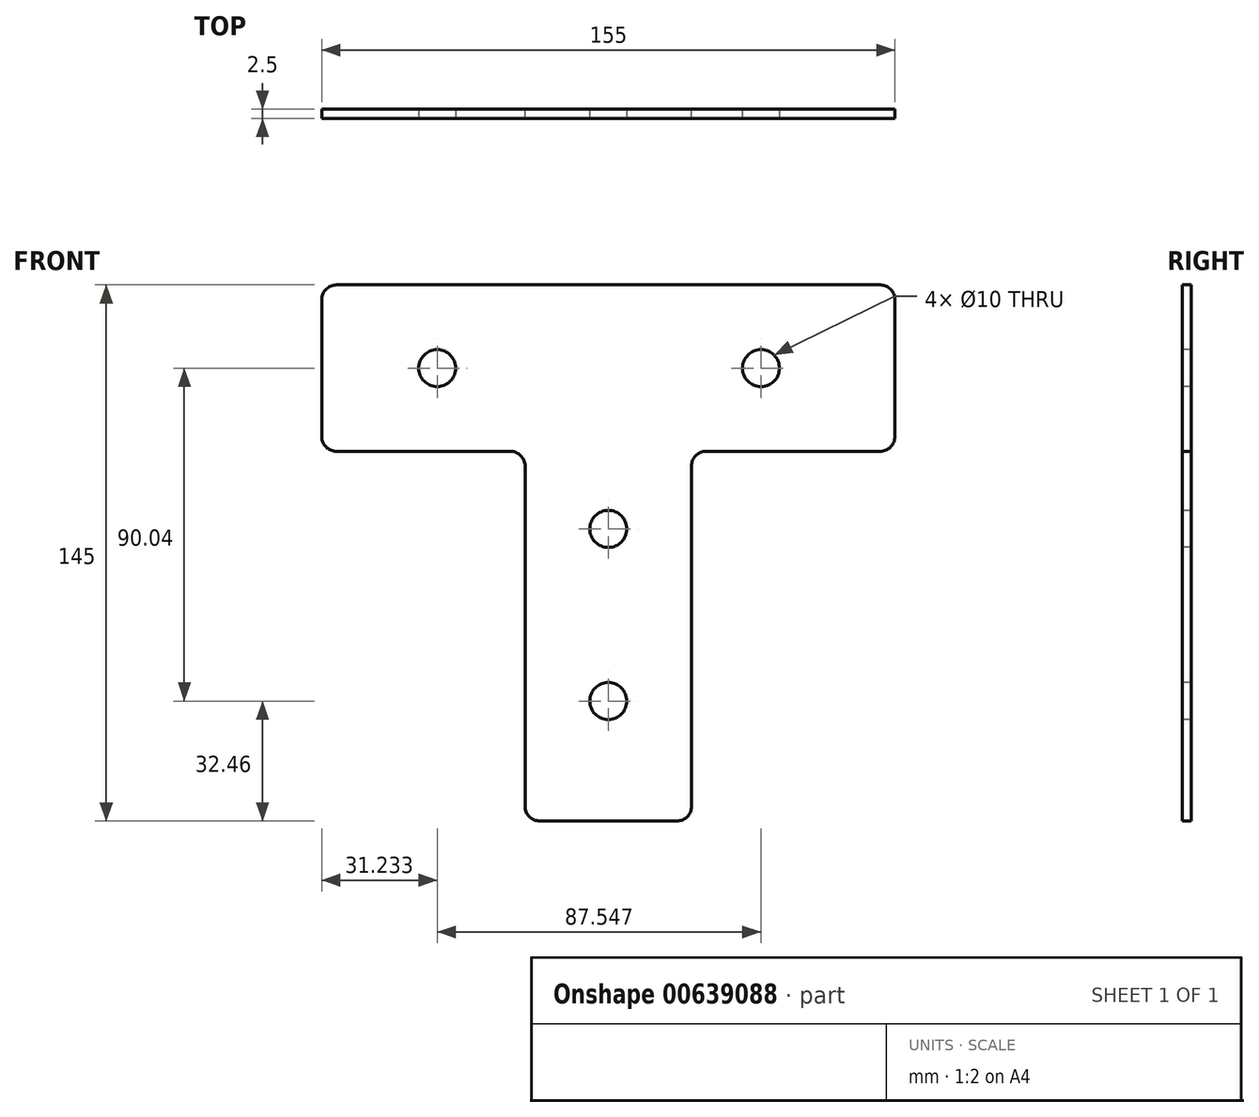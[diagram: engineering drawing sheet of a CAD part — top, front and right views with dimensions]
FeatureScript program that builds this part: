
annotation { "Feature Type Name" : "Feature", "Feature Type Description" : "" }
export const myFeature = defineFeature(function(context is Context, id is Id, definition is map)
    precondition{}
    {
        {
            var Q0;
            Q0=qCreatedBy(makeId("Front.planeOp"),FACE);
            var sketch = newSketch(context, id + "F0", { "sketchPlane" : qUnion([Q0])});
            skLineSegment(sketch, "E0.bottom", {"start": v(73.5, 22.5) * mm, "end": v(-73.5, 22.5) * mm});
            skLineSegment(sketch, "E0.top", {"start": v(77.5, -22.5) * mm, "end": v(22.5, -22.5) * mm});
            skLineSegment(sketch, "E0.left", {"start": v(77.5, 18.5) * mm, "end": v(77.5, -18.5) * mm});
            skLineSegment(sketch, "E0.right", {"start": v(-77.5, 18.5) * mm, "end": v(-77.5, -18.5) * mm});
            skPoint(sketch, "E0.middle", {"position": v(0, 0) * mm});
            skLineSegment(sketch, "E1", {"start": v(73.5, -22.5) * mm, "end": v(26.5, -22.5) * mm});
            skLineSegment(sketch, "E2", {"start": v(22.5, -26.5) * mm, "end": v(22.5, -118.5) * mm});
            skLineSegment(sketch, "E3", {"start": v(18.5, -122.5) * mm, "end": v(-18.5, -122.5) * mm});
            skLineSegment(sketch, "E4", {"start": v(-22.5, -118.5) * mm, "end": v(-22.5, -26.5) * mm});
            skLineSegment(sketch, "E5", {"start": v(-22.5, -22.5) * mm, "end": v(-77.5, -22.5) * mm});
            skLineSegment(sketch, "E6.trimOffspring", {"start": v(-26.5, -22.5) * mm, "end": v(-73.5, -22.5) * mm});
            skPoint(sketch, "E7.visualSharp", {"position": v(-77.5, 22.5) * mm});
            skArc(sketch, "E7.filletArc", {"start": v(-73.5, 22.5) * mm, "mid": v(-76.33, 21.33) * mm, "end": v(-77.5, 18.5) * mm});
            skPoint(sketch, "E8.visualSharp", {"position": v(-77.5, -22.5) * mm});
            skArc(sketch, "E8.filletArc", {"start": v(-77.5, -18.5) * mm, "mid": v(-76.33, -21.33) * mm, "end": v(-73.5, -22.5) * mm});
            skPoint(sketch, "E9.visualSharp", {"position": v(77.5, 22.5) * mm});
            skArc(sketch, "E9.filletArc", {"start": v(77.5, 18.5) * mm, "mid": v(76.33, 21.33) * mm, "end": v(73.5, 22.5) * mm});
            skPoint(sketch, "E10.visualSharp", {"position": v(77.5, -22.5) * mm});
            skArc(sketch, "E10.filletArc", {"start": v(73.5, -22.5) * mm, "mid": v(76.33, -21.33) * mm, "end": v(77.5, -18.5) * mm});
            skPoint(sketch, "E11.visualSharp", {"position": v(22.5, -22.5) * mm});
            skArc(sketch, "E11.filletArc", {"start": v(26.5, -22.5) * mm, "mid": v(23.67, -23.67) * mm, "end": v(22.5, -26.5) * mm});
            skPoint(sketch, "E12.visualSharp", {"position": v(22.5, -122.5) * mm});
            skArc(sketch, "E12.filletArc", {"start": v(18.5, -122.5) * mm, "mid": v(21.33, -121.33) * mm, "end": v(22.5, -118.5) * mm});
            skPoint(sketch, "E13.visualSharp", {"position": v(-22.5, -122.5) * mm});
            skArc(sketch, "E13.filletArc", {"start": v(-22.5, -118.5) * mm, "mid": v(-21.33, -121.33) * mm, "end": v(-18.5, -122.5) * mm});
            skPoint(sketch, "E14.visualSharp", {"position": v(-22.5, -22.5) * mm});
            skArc(sketch, "E14.filletArc", {"start": v(-22.5, -26.5) * mm, "mid": v(-23.67, -23.67) * mm, "end": v(-26.5, -22.5) * mm});
            skSolve(sketch);
        }
        {
            var Q0;
            Q0 = qSketchRegion(id + "F0", true);
            extrude(context, id + "F1", {"entities" : qUnion([Q0]), "depth" : 2.5 * mm, "offsetDistance" : 25 * mm});
        }
        {
            var Q0;
            Q0=makeQuery(id+"F1.opExtrude","CAP_FACE",FACE,{"disambiguationData":[OSD([sQuery(id+"F0.wireOp",EDGE,"E0.bottom"),sQuery(id+"F0.wireOp",EDGE,"E0.left"),sQuery(id+"F0.wireOp",EDGE,"E0.right"),sQuery(id+"F0.wireOp",EDGE,"E1"),sQuery(id+"F0.wireOp",EDGE,"E2"),sQuery(id+"F0.wireOp",EDGE,"E3"),sQuery(id+"F0.wireOp",EDGE,"E4"),sQuery(id+"F0.wireOp",EDGE,"E6.trimOffspring"),sQuery(id+"F0.wireOp",EDGE,"E7.filletArc"),sQuery(id+"F0.wireOp",EDGE,"E8.filletArc"),sQuery(id+"F0.wireOp",EDGE,"E9.filletArc"),sQuery(id+"F0.wireOp",EDGE,"E10.filletArc"),sQuery(id+"F0.wireOp",EDGE,"E11.filletArc"),sQuery(id+"F0.wireOp",EDGE,"E12.filletArc"),sQuery(id+"F0.wireOp",EDGE,"E13.filletArc"),sQuery(id+"F0.wireOp",EDGE,"E14.filletArc")])],"isStart":false});
            var sketch = newSketch(context, id + "F2", { "sketchPlane" : qUnion([Q0])});
            skCircle(sketch, "E15", {"center": v(-46.27, 0) * mm, "radius": 5 * mm});
            skCircle(sketch, "E16", {"center": v(41.28, 0) * mm, "radius": 5 * mm});
            skCircle(sketch, "E17", {"center": v(0, -43.5) * mm, "radius": 5 * mm});
            skCircle(sketch, "E18", {"center": v(0, -90.04) * mm, "radius": 5 * mm});
            skSolve(sketch);
        }
        {
            var Q0;
            Q0=makeQuery(id+"F2.imprint","IMPRINT",FACE,{"disambiguationData":[TD([[makeQuery(id+"F2.imprint","IMPRINT",EDGE,{"derivedFrom":sQuery(id+"F2.wireOp",EDGE,"E15")}),1.0]])]});
            var Q1;
            Q1=makeQuery(id+"F2.imprint","IMPRINT",FACE,{"disambiguationData":[TD([[makeQuery(id+"F2.imprint","IMPRINT",EDGE,{"derivedFrom":sQuery(id+"F2.wireOp",EDGE,"E16")}),1.0]])]});
            var Q2;
            Q2=makeQuery(id+"F2.imprint","IMPRINT",FACE,{"disambiguationData":[TD([[makeQuery(id+"F2.imprint","IMPRINT",EDGE,{"derivedFrom":sQuery(id+"F2.wireOp",EDGE,"E17")}),1.0]])]});
            var Q3;
            Q3=makeQuery(id+"F2.imprint","IMPRINT",FACE,{"disambiguationData":[TD([[makeQuery(id+"F2.imprint","IMPRINT",EDGE,{"derivedFrom":sQuery(id+"F2.wireOp",EDGE,"E18")}),1.0]])]});
            extrude(context, id + "F3", {"entities" : qUnion([Q0, Q1, Q2, Q3]), "operationType" : NewBodyOperationType.REMOVE, "endBound" : BoundingType.THROUGH_ALL, "oppositeDirection" : true, "depth" : 25 * mm, "offsetDistance" : 25 * mm});
        }
    });
